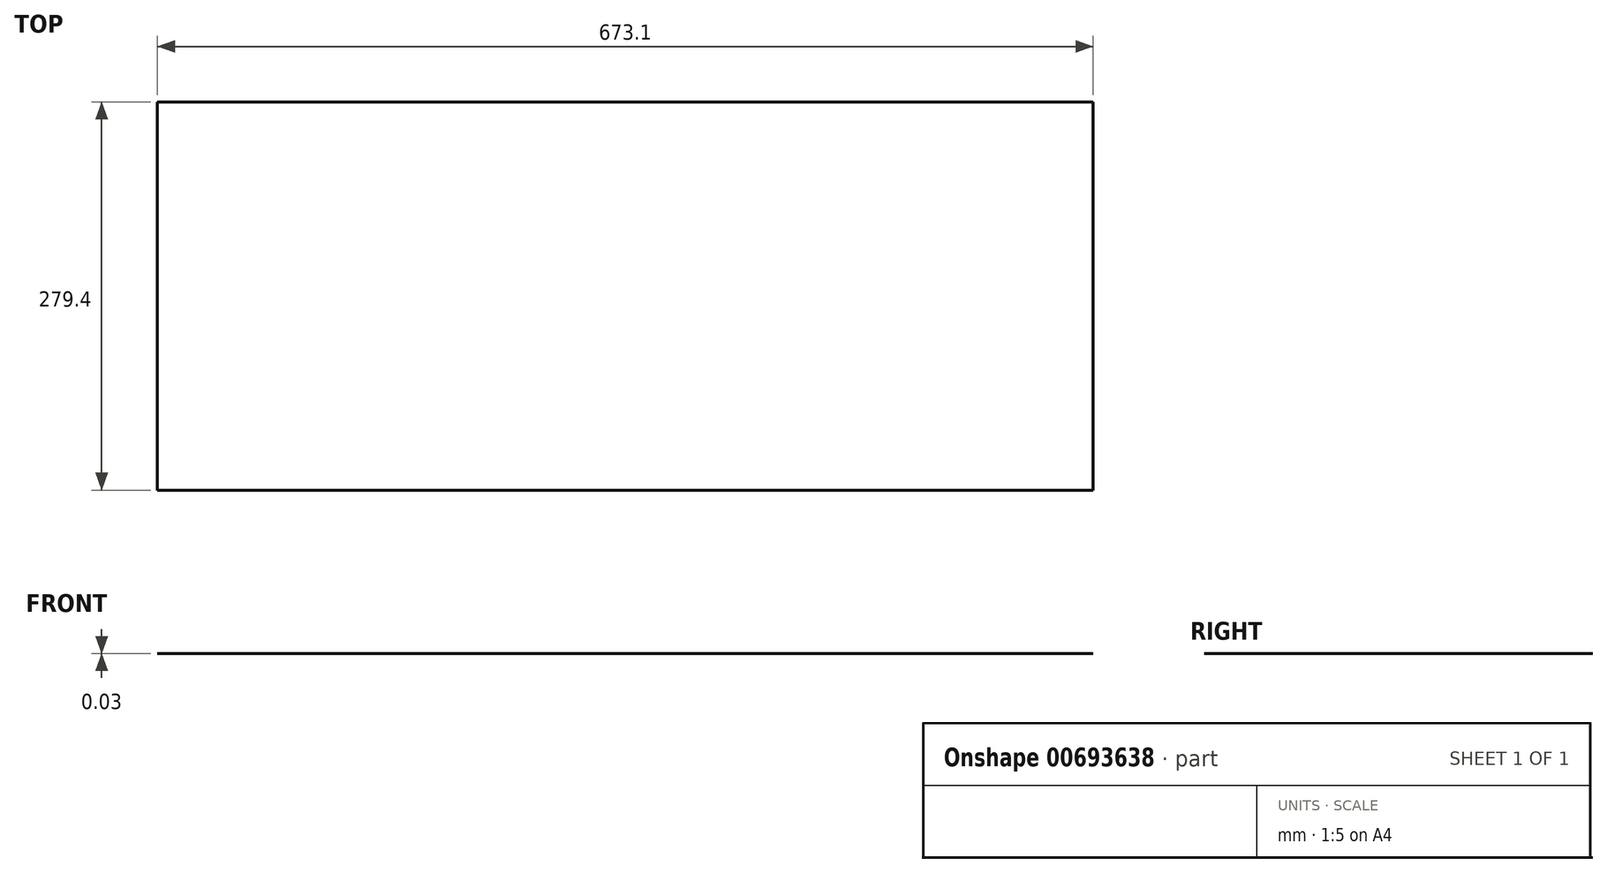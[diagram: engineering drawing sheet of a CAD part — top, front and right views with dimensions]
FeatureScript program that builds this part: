
annotation { "Feature Type Name" : "Feature", "Feature Type Description" : "" }
export const myFeature = defineFeature(function(context is Context, id is Id, definition is map)
    precondition{}
    {
        {
            var Q0;
            Q0=qCreatedBy(makeId("Top.planeOp"),FACE);
            var sketch = newSketch(context, id + "F0", { "sketchPlane" : qUnion([Q0])});
            skLineSegment(sketch, "E0.bottom", {"start": v(-336.55, 139.7) * mm, "end": v(336.55, 139.7) * mm});
            skLineSegment(sketch, "E0.top", {"start": v(-336.55, -139.7) * mm, "end": v(336.55, -139.7) * mm});
            skLineSegment(sketch, "E0.left", {"start": v(-336.55, 139.7) * mm, "end": v(-336.55, -139.7) * mm});
            skLineSegment(sketch, "E0.right", {"start": v(336.55, 139.7) * mm, "end": v(336.55, -139.7) * mm});
            skPoint(sketch, "E0.middle", {"position": v(0, 0) * mm});
            skSolve(sketch);
        }
        {
            var Q0;
            Q0=makeQuery(id+"F0.imprint","IMPRINT",FACE,{"disambiguationData":[TD([[makeQuery(id+"F0.imprint","IMPRINT",EDGE,{"derivedFrom":sQuery(id+"F0.wireOp",EDGE,"E0.bottom")}),-1.0]])]});
            extrude(context, id + "F1", {"entities" : qUnion([Q0]), "depth" : 3 / 101.6 * mm});
        }
    });
